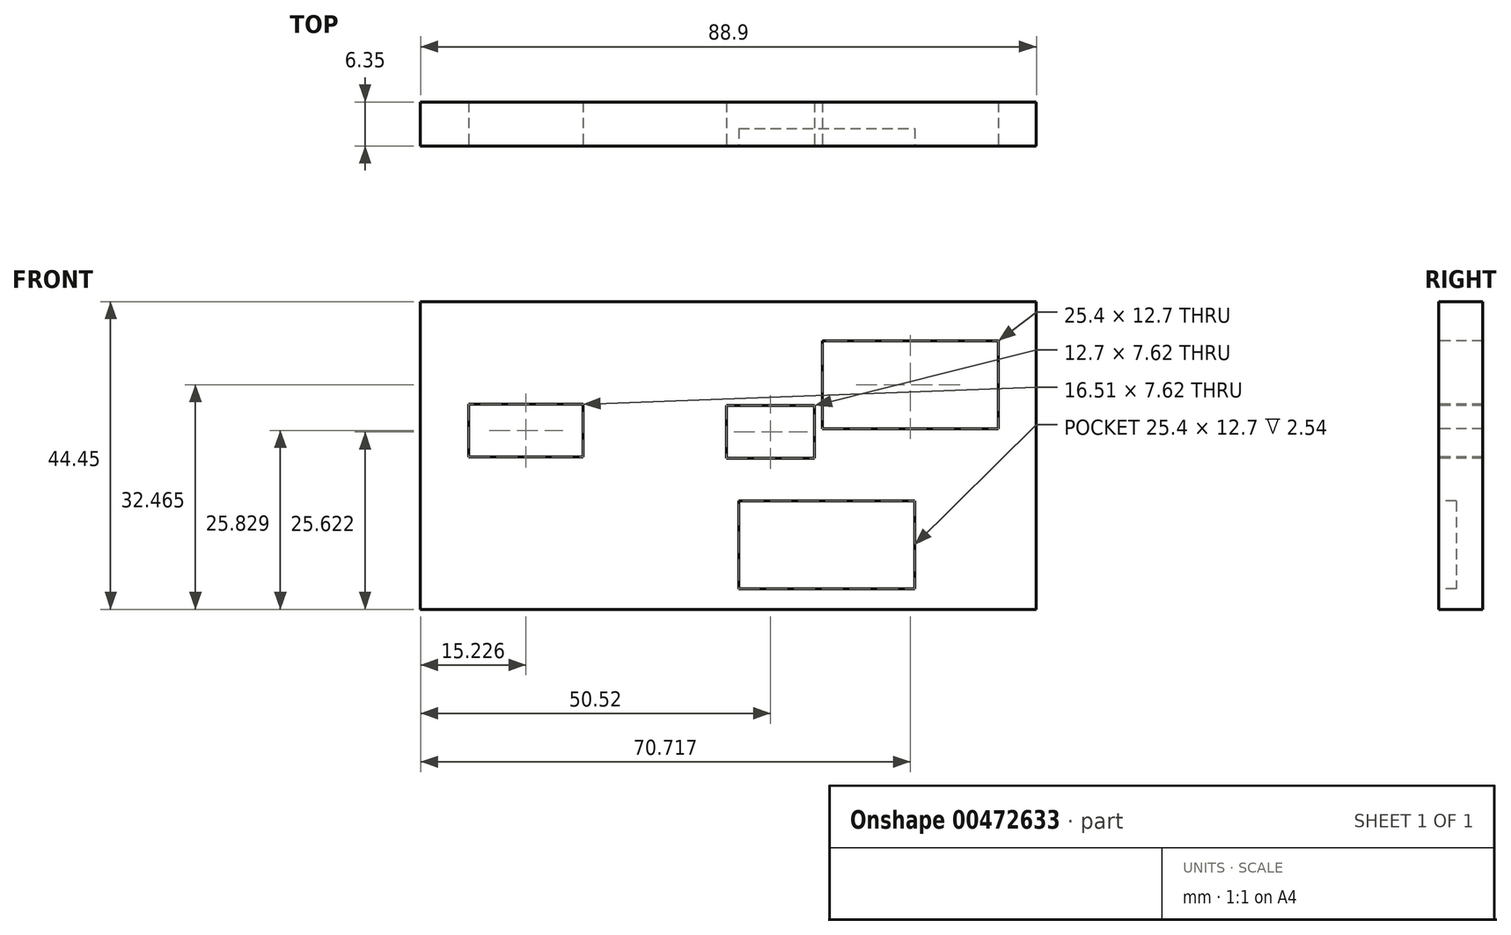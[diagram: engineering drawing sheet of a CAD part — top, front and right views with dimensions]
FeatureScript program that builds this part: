
annotation { "Feature Type Name" : "Feature", "Feature Type Description" : "" }
export const myFeature = defineFeature(function(context is Context, id is Id, definition is map)
    precondition{}
    {
        {
            var Q0;
            Q0=qCreatedBy(makeId("Front.planeOp"),FACE);
            var sketch = newSketch(context, id + "F0", { "sketchPlane" : qUnion([Q0])});
            skLineSegment(sketch, "E0.bottom", {"start": v(-44.17, 28.85) * mm, "end": v(44.73, 28.85) * mm});
            skLineSegment(sketch, "E0.top", {"start": v(-44.17, -15.6) * mm, "end": v(44.73, -15.6) * mm});
            skLineSegment(sketch, "E0.left", {"start": v(-44.17, 28.85) * mm, "end": v(-44.17, -15.6) * mm});
            skLineSegment(sketch, "E0.right", {"start": v(44.73, 28.85) * mm, "end": v(44.73, -15.6) * mm});
            skSolve(sketch);
        }
        {
            var Q0;
            Q0=makeQuery(id+"F0.imprint","IMPRINT",FACE,{"disambiguationData":[TD([[makeQuery(id+"F0.imprint","IMPRINT",EDGE,{"derivedFrom":sQuery(id+"F0.wireOp",EDGE,"E0.bottom")}),-1.0]])]});
            extrude(context, id + "F1", {"entities" : qUnion([Q0]), "depth" : 6.35 * mm});
        }
        {
            var Q0;
            Q0=makeQuery(id+"F1.opExtrude","CAP_FACE",FACE,{"disambiguationData":[OSD([sQuery(id+"F0.wireOp",EDGE,"E0.bottom"),sQuery(id+"F0.wireOp",EDGE,"E0.top"),sQuery(id+"F0.wireOp",EDGE,"E0.left"),sQuery(id+"F0.wireOp",EDGE,"E0.right")])],"isStart":false});
            var sketch = newSketch(context, id + "F2", { "sketchPlane" : qUnion([Q0])});
            skLineSegment(sketch, "E1.bottom", {"start": v(13.85, 23.22) * mm, "end": v(39.25, 23.22) * mm});
            skLineSegment(sketch, "E1.top", {"start": v(13.85, 10.52) * mm, "end": v(39.25, 10.52) * mm});
            skLineSegment(sketch, "E1.left", {"start": v(13.85, 23.22) * mm, "end": v(13.85, 10.52) * mm});
            skLineSegment(sketch, "E1.right", {"start": v(39.25, 23.22) * mm, "end": v(39.25, 10.52) * mm});
            skSolve(sketch);
        }
        {
            var Q0;
            Q0=makeQuery(id+"F2.imprint","IMPRINT",FACE,{"disambiguationData":[TD([[makeQuery(id+"F2.imprint","IMPRINT",EDGE,{"derivedFrom":sQuery(id+"F2.wireOp",EDGE,"E1.bottom")}),-1.0]])]});
            var Q1;
            Q1=sQuery(id+"F2.wireOp",EDGE,"E1.left");
            var Q2;
            Q2=sQuery(id+"F2.wireOp",EDGE,"E1.bottom");
            var Q3;
            Q3=sQuery(id+"F2.wireOp",EDGE,"E1.top");
            var Q4;
            Q4=sQuery(id+"F2.wireOp",EDGE,"E1.right");
            extrude(context, id + "F3", {"entities" : qUnion([Q0]), "operationType" : NewBodyOperationType.REMOVE, "surfaceEntities" : qUnion([Q1, Q2, Q3, Q4]), "endBound" : BoundingType.THROUGH_ALL, "oppositeDirection" : true, "depth" : 25.4 * mm});
        }
        {
            var Q0;
            Q0=makeQuery(id+"F1.opExtrude","CAP_FACE",FACE,{"disambiguationData":[OSD([sQuery(id+"F0.wireOp",EDGE,"E0.bottom"),sQuery(id+"F0.wireOp",EDGE,"E0.top"),sQuery(id+"F0.wireOp",EDGE,"E0.left"),sQuery(id+"F0.wireOp",EDGE,"E0.right")])],"isStart":false});
            var sketch = newSketch(context, id + "F4", { "sketchPlane" : qUnion([Q0])});
            skLineSegment(sketch, "E2.bottom", {"start": v(0, 13.83) * mm, "end": v(12.7, 13.83) * mm});
            skLineSegment(sketch, "E2.top", {"start": v(0, 6.21) * mm, "end": v(12.7, 6.21) * mm});
            skLineSegment(sketch, "E2.left", {"start": v(0, 13.83) * mm, "end": v(0, 6.21) * mm});
            skLineSegment(sketch, "E2.right", {"start": v(12.7, 13.83) * mm, "end": v(12.7, 6.21) * mm});
            skSolve(sketch);
        }
        {
            var Q0;
            Q0=makeQuery(id+"F4.imprint","IMPRINT",FACE,{"disambiguationData":[TD([[makeQuery(id+"F4.imprint","IMPRINT",EDGE,{"derivedFrom":sQuery(id+"F4.wireOp",EDGE,"E2.bottom")}),-1.0]])]});
            extrude(context, id + "F5", {"entities" : qUnion([Q0]), "operationType" : NewBodyOperationType.REMOVE, "endBound" : BoundingType.THROUGH_ALL, "oppositeDirection" : true, "depth" : 25.4 * mm});
        }
        {
            var Q0;
            Q0=makeQuery(id+"F1.opExtrude","CAP_FACE",FACE,{"disambiguationData":[OSD([sQuery(id+"F0.wireOp",EDGE,"E0.bottom"),sQuery(id+"F0.wireOp",EDGE,"E0.top"),sQuery(id+"F0.wireOp",EDGE,"E0.left"),sQuery(id+"F0.wireOp",EDGE,"E0.right")])],"isStart":false});
            var sketch = newSketch(context, id + "F6", { "sketchPlane" : qUnion([Q0])});
            skLineSegment(sketch, "E3.bottom", {"start": v(1.77, 0.06) * mm, "end": v(27.17, 0.06) * mm});
            skLineSegment(sketch, "E3.top", {"start": v(1.77, -12.64) * mm, "end": v(27.17, -12.64) * mm});
            skLineSegment(sketch, "E3.left", {"start": v(1.77, 0.06) * mm, "end": v(1.77, -12.64) * mm});
            skLineSegment(sketch, "E3.right", {"start": v(27.17, 0.06) * mm, "end": v(27.17, -12.64) * mm});
            skSolve(sketch);
        }
        {
            var Q0;
            Q0=makeQuery(id+"F6.imprint","IMPRINT",FACE,{"disambiguationData":[TD([[makeQuery(id+"F6.imprint","IMPRINT",EDGE,{"derivedFrom":sQuery(id+"F6.wireOp",EDGE,"E3.bottom")}),-1.0]])]});
            extrude(context, id + "F7", {"entities" : qUnion([Q0]), "operationType" : NewBodyOperationType.REMOVE, "oppositeDirection" : true, "depth" : 2.54 * mm});
        }
        {
            var Q0;
            Q0=makeQuery(id+"F1.opExtrude","CAP_FACE",FACE,{"disambiguationData":[OSD([sQuery(id+"F0.wireOp",EDGE,"E0.bottom"),sQuery(id+"F0.wireOp",EDGE,"E0.top"),sQuery(id+"F0.wireOp",EDGE,"E0.left"),sQuery(id+"F0.wireOp",EDGE,"E0.right")])],"isStart":false});
            var sketch = newSketch(context, id + "F8", { "sketchPlane" : qUnion([Q0])});
            skLineSegment(sketch, "E4.bottom", {"start": v(-37.2, 14.04) * mm, "end": v(-20.69, 14.04) * mm});
            skLineSegment(sketch, "E4.top", {"start": v(-37.2, 6.42) * mm, "end": v(-20.69, 6.42) * mm});
            skLineSegment(sketch, "E4.left", {"start": v(-37.2, 14.04) * mm, "end": v(-37.2, 6.42) * mm});
            skLineSegment(sketch, "E4.right", {"start": v(-20.69, 14.04) * mm, "end": v(-20.69, 6.42) * mm});
            skSolve(sketch);
        }
        {
            var Q0;
            Q0=makeQuery(id+"F8.imprint","IMPRINT",FACE,{"disambiguationData":[TD([[makeQuery(id+"F8.imprint","IMPRINT",EDGE,{"derivedFrom":sQuery(id+"F8.wireOp",EDGE,"E4.bottom")}),-1.0]])]});
            extrude(context, id + "F9", {"entities" : qUnion([Q0]), "operationType" : NewBodyOperationType.REMOVE, "endBound" : BoundingType.THROUGH_ALL, "oppositeDirection" : true, "depth" : 25.4 * mm});
        }
    });
